FCSTD DOCUMENT  (FreeCAD 0.19R24366 (Git))
Label: hulltest2
License: All rights reserved
LicenseURL: http://en.wikipedia.org/wiki/All_rights_reserved
objects: Sketcher::SketchObject×3, PartDesign::Body×1
note: 4 computed .brp shape members not serialized (recipe doc carries the construction recipe); baked Part::Feature solids carry a one-line shape summary decoded from their .brp

FEATURE [Sketcher::SketchObject] Sketch  label="HullOutline"
  FullyConstrained = true
  Placement = pos=(0,0,0) rot=(0.980944,0.137386,0.137386;1.59004rad)
  Support = -> [XZ_Plane]
  sketch-geometry (8):
    g0: LineSegment StartX=0 StartY=0 StartZ=0 EndX=160 EndY=3 EndZ=0
    g1: LineSegment StartX=0 StartY=0 StartZ=0 EndX=-20 EndY=70 EndZ=0
    g2: LineSegment StartX=-20 StartY=70 StartZ=0 EndX=-170 EndY=70 EndZ=0
    g3: LineSegment StartX=-170 StartY=70 StartZ=0 EndX=-190 EndY=150 EndZ=0
    g4: LineSegment StartX=-190 StartY=150 StartZ=0 EndX=420 EndY=150 EndZ=0
    g5: LineSegment StartX=420 StartY=150 StartZ=0 EndX=180 EndY=70 EndZ=0
    g6: LineSegment StartX=180 StartY=70 StartZ=0 EndX=160 EndY=3 EndZ=0
    g7: LineSegment StartX=-20 StartY=70 StartZ=0 EndX=180 EndY=70 EndZ=0
  constraints (22):
    c: Coincident(g1,g0)
    c: Horizontal(g2)
    c: Coincident(g3,g2)
    c: Horizontal(g4)
    c: Coincident(g6,g5)
    c: Coincident(g6,g0)
    c: DistanceX(g4,g4) = 610
    c: Coincident(g3,g4)
    c: DistanceX(g3,g2) = 20
    c: DistanceX(g2,g1) = 150
    c: Coincident(g2,g1)
    c: DistanceY(g0,g1) = 70
    c: DistanceX(g0,g0) = 160
    c: DistanceX(g1,g0) = 20
    c: DistanceY(g2,g3) = 80
    c: DistanceY(g0,g0) = 3
    c: Horizontal(g1,g5)
    c: DistanceX(g0,g5) = 20
    c: Coincident(g5,g4)
    c: Coincident(g-1,g0)
    c: Coincident(g7,g1)
    c: Coincident(g7,g5)
FEATURE [Sketcher::SketchObject] Sketch004  label="Segment1"
  ExternalGeometry = -> [Sketch]
  FullyConstrained = true
  MapMode = 5
  Placement = pos=(0,0,0) rot=(0.57735,0.57735,0.57735;2.0944rad)
  Support = -> [YZ_Plane]
  sketch-geometry (36):
    g0: LineSegment StartX=0 StartY=90.7889 StartZ=0 EndX=0 EndY=61.1833 EndZ=0
    g1: LineSegment StartX=0 StartY=90.7889 StartZ=0 EndX=0 EndY=120.394 EndZ=0
    g2: LineSegment StartX=0 StartY=31.5778 StartZ=0 EndX=0 EndY=61.1833 EndZ=0
    g3: LineSegment StartX=0 StartY=31.5778 StartZ=0 EndX=0 EndY=1.9722 EndZ=0
    g4: LineSegment StartX=0 StartY=31.5778 StartZ=0 EndX=51.2783 EndY=31.5778 EndZ=0
    g5: LineSegment StartX=0 StartY=61.1833 StartZ=0 EndX=102.557 EndY=61.1833 EndZ=0
    g6: LineSegment StartX=0 StartY=90.7889 StartZ=0 EndX=130 EndY=90.7889 EndZ=0
    g7: LineSegment StartX=0 StartY=120.394 StartZ=0 EndX=136.742 EndY=120.394 EndZ=0
    g8: Circle CenterX=68.3711 CenterY=120.394 CenterZ=0 NormalX=0 NormalY=0 NormalZ=1 AngleXU=0 Radius=68.3711
    g9: LineSegment StartX=0 StartY=120.394 StartZ=0 EndX=0 EndY=150 EndZ=0
    g10: LineSegment StartX=0 StartY=150 StartZ=0 EndX=130 EndY=150 EndZ=0
    g11: LineSegment StartX=0 StartY=1.9722 StartZ=0 EndX=102.557 EndY=61.1833 EndZ=0
    g12: LineSegment StartX=0 StartY=61.1833 StartZ=0 EndX=0 EndY=90.7889 EndZ=0
    g13: LineSegment StartX=0 StartY=31.5778 StartZ=0 EndX=0 EndY=61.1833 EndZ=0
    g14: LineSegment StartX=-40 StartY=90.7889 StartZ=0 EndX=-40 EndY=61.1833 EndZ=0
    g15: LineSegment StartX=-40 StartY=90.7889 StartZ=0 EndX=-40 EndY=120.394 EndZ=0
    g16: LineSegment StartX=-40 StartY=31.5778 StartZ=0 EndX=-40 EndY=61.1833 EndZ=0
    g17: LineSegment StartX=-40 StartY=31.5778 StartZ=0 EndX=-40 EndY=1.9722 EndZ=0
    g18: LineSegment StartX=-40 StartY=31.5778 StartZ=0 EndX=-91.2783 EndY=31.5778 EndZ=0
    g19: LineSegment StartX=-40 StartY=61.1833 StartZ=0 EndX=-142.557 EndY=61.1833 EndZ=0
    g20: LineSegment StartX=-40 StartY=90.7889 StartZ=0 EndX=-170 EndY=90.7889 EndZ=0
    g21: LineSegment StartX=-40 StartY=120.394 StartZ=0 EndX=-176.742 EndY=120.394 EndZ=0
    g22: Circle CenterX=-108.371 CenterY=120.394 CenterZ=0 NormalX=0 NormalY=0 NormalZ=1 AngleXU=0 Radius=68.3711
    g23: LineSegment StartX=-40 StartY=120.394 StartZ=0 EndX=-40 EndY=150 EndZ=0
    g24: LineSegment StartX=-40 StartY=150 StartZ=0 EndX=-170 EndY=150 EndZ=0
    g25: LineSegment StartX=-40 StartY=61.1833 StartZ=0 EndX=-40 EndY=90.7889 EndZ=0
    g26: LineSegment StartX=-40 StartY=31.5778 StartZ=0 EndX=-40 EndY=61.1833 EndZ=0
    g27: LineSegment StartX=0 StartY=0 StartZ=0 EndX=-40 EndY=0 EndZ=0
    g28: LineSegment StartX=-142.557 StartY=61.1833 StartZ=0 EndX=-40 EndY=1.9722 EndZ=0
    g29: LineSegment StartX=-40 StartY=150 StartZ=0 EndX=0 EndY=150 EndZ=0
    g30: LineSegment StartX=-40 StartY=0 StartZ=0 EndX=-20 EndY=-9.32615 EndZ=0
    g31: LineSegment StartX=-20 StartY=-9.32615 StartZ=0 EndX=0 EndY=0 EndZ=0
    g32: LineSegment StartX=-40 StartY=1.9722 StartZ=0 EndX=-40 EndY=0 EndZ=0
    g33: LineSegment StartX=0 StartY=1.9722 StartZ=0 EndX=0 EndY=0 EndZ=0
    g34: LineSegment StartX=-40 StartY=150 StartZ=0 EndX=0 EndY=150 EndZ=0
    g35: LineSegment StartX=-170 StartY=150 StartZ=0 EndX=-40 EndY=150 EndZ=0
  constraints (102):
    c: PointOnObject(g10,g8)
    c: PointOnObject(g7,g8)
    c: PointOnObject(g5,g8)
    c: PointOnObject(g4,g11)
    c: Coincident(g9,g10)
    c: Coincident(g1,g7)
    c: Coincident(g1,g9)
    c: Coincident(g1,g6)
    c: Coincident(g1,g12)
    c: Coincident(g2,g3)
    c: Coincident(g2,g4)
    c: Coincident(g3,g11)
    c: Vertical(g3)
    c: Vertical(g2)
    c: Vertical(g0)
    c: Vertical(g12)
    c: Vertical(g1)
    c: Vertical(g9)
    c: Coincident(g0,g5)
    c: Horizontal(g4)
    c: Coincident(g5,g11)
    c: Horizontal(g5)
    c: Tangent(g11,g8)
    c: Horizontal(g6)
    c: Horizontal(g7)
    c: Horizontal(g10)
    c: Coincident(g0,g12)
    c: Equal(g3,g2)
    c: Equal(g2,g0)
    c: Equal(g0,g12)
    c: Equal(g12,g1)
    c: PointOnObject(g1,g8)
    c: Tangent(g1,g8)
    c: PointOnObject(g6,g8)
    c: Coincident(g13,g2)
    c: Coincident(g13,g0)
    c: Equal(g13,g0)
    c: Vertical(g13)
    c: Equal(g9,g1)
    c: PointOnObject(g24,g22)
    c: PointOnObject(g21,g22)
    c: PointOnObject(g19,g22)
    c: Coincident(g23,g24)
    c: Coincident(g15,g21)
    c: Coincident(g15,g23)
    c: Coincident(g15,g20)
    c: Coincident(g15,g25)
    c: Coincident(g16,g17)
    c: Coincident(g16,g18)
    c: Vertical(g17)
    c: Vertical(g16)
    c: Vertical(g14)
    c: Vertical(g25)
    c: Vertical(g15)
    c: Vertical(g23)
    c: Coincident(g14,g19)
    c: Horizontal(g18)
    c: Horizontal(g19)
    c: Horizontal(g20)
    c: Horizontal(g21)
    c: Horizontal(g24)
    c: Coincident(g14,g25)
    c: Equal(g16,g14)
    c: Equal(g14,g25)
    c: Equal(g25,g15)
    c: PointOnObject(g15,g22)
    c: Tangent(g15,g22)
    c: PointOnObject(g20,g22)
    c: Coincident(g26,g16)
    c: Coincident(g26,g14)
    c: Equal(g26,g14)
    c: Vertical(g26)
    c: Equal(g23,g15)
    c: Equal(g21,g7)
    c: Horizontal(g27)
    c: Coincident(g28,g19)
    c: Coincident(g28,g17)
    c: PointOnObject(g18,g28)
    c: Tangent(g28,g22)
    c: Coincident(g29,g23)
    c: Coincident(g29,g9)
    c: Horizontal(g29)
    c: Angle(g31,g30) = 2.26893
    c: Coincident(g30,g31)
    c: Coincident(g27,g30)
    c: Coincident(g31,g27)
    c: Coincident(g32,g17)
    c: Coincident(g32,g30)
    c: Vertical(g32)
    c: Coincident(g33,g3)
    c: Coincident(g33,g31)
    c: Vertical(g33)
    c: Coincident(g34,g23)
    c: Coincident(g35,g24)
    c: DistanceX(g27,g27) = 40
    c: DistanceX(g30,g31) = 20
    c: Coincident(g34,g9)
    c: Coincident(g35,g23)
    c: Horizontal(g-7,g9)
    c: Coincident(g-1,g31)
    c: DistanceX(g24,g10) = 300
    c: Horizontal(g2,g-3)
FEATURE [Sketcher::SketchObject] Sketch006  label="Segment002"
  ExternalGeometry = -> [Sketch]
  FullyConstrained = false
  MapMode = 1
  Placement = pos=(153.844,43.9554,3) rot=(0.57735,0.57735,0.57735;2.0944rad)
  Support = -> [Sketch]
  sketch-geometry (36):
    g0: LineSegment StartX=0 StartY=72.2178 StartZ=0 EndX=0 EndY=43.0677 EndZ=0
    g1: LineSegment StartX=0 StartY=72.2178 StartZ=0 EndX=0 EndY=101.368 EndZ=0
    g2: LineSegment StartX=0 StartY=13.9176 StartZ=0 EndX=0 EndY=43.0677 EndZ=0
    g3: LineSegment StartX=0 StartY=13.9176 StartZ=0 EndX=0 EndY=-15.2325 EndZ=0
    g4: LineSegment StartX=0 StartY=13.9176 StartZ=0 EndX=50.4894 EndY=13.9176 EndZ=0
    g5: LineSegment StartX=0 StartY=43.0677 StartZ=0 EndX=100.979 EndY=43.0677 EndZ=0
    g6: LineSegment StartX=0 StartY=72.2178 StartZ=0 EndX=128 EndY=72.2178 EndZ=0
    g7: LineSegment StartX=0 StartY=101.368 StartZ=0 EndX=134.638 EndY=101.368 EndZ=0
    g8: Circle CenterX=67.3192 CenterY=101.368 CenterZ=0 NormalX=0 NormalY=0 NormalZ=1 AngleXU=0 Radius=67.3192
    g9: LineSegment StartX=0 StartY=101.368 StartZ=0 EndX=0 EndY=130.518 EndZ=0
    g10: LineSegment StartX=0 StartY=130.518 StartZ=0 EndX=128 EndY=130.518 EndZ=0
    g11: LineSegment StartX=0 StartY=-15.2325 StartZ=0 EndX=100.979 EndY=43.0677 EndZ=0
    g12: LineSegment StartX=0 StartY=43.0677 StartZ=0 EndX=0 EndY=72.2178 EndZ=0
    g13: LineSegment StartX=0 StartY=13.9176 StartZ=0 EndX=0 EndY=43.0677 EndZ=0
    g14: LineSegment StartX=-40 StartY=72.2178 StartZ=0 EndX=-40 EndY=43.0677 EndZ=0
    g15: LineSegment StartX=-40 StartY=72.2178 StartZ=0 EndX=-40 EndY=101.368 EndZ=0
    g16: LineSegment StartX=-40 StartY=13.9176 StartZ=0 EndX=-40 EndY=43.0677 EndZ=0
    g17: LineSegment StartX=-40 StartY=13.9176 StartZ=0 EndX=-40 EndY=-15.2325 EndZ=0
    g18: LineSegment StartX=-40 StartY=13.9176 StartZ=0 EndX=-90.4894 EndY=13.9176 EndZ=0
    g19: LineSegment StartX=-40 StartY=43.0677 StartZ=0 EndX=-140.979 EndY=43.0677 EndZ=0
    g20: LineSegment StartX=-40 StartY=72.2178 StartZ=0 EndX=-168 EndY=72.2178 EndZ=0
    g21: LineSegment StartX=-40 StartY=101.368 StartZ=0 EndX=-174.638 EndY=101.368 EndZ=0
    g22: Circle CenterX=-107.319 CenterY=101.368 CenterZ=0 NormalX=0 NormalY=0 NormalZ=1 AngleXU=0 Radius=67.3192
    g23: LineSegment StartX=-40 StartY=101.368 StartZ=0 EndX=-40 EndY=130.518 EndZ=0
    g24: LineSegment StartX=-40 StartY=130.518 StartZ=0 EndX=-168 EndY=130.518 EndZ=0
    g25: LineSegment StartX=-40 StartY=43.0677 StartZ=0 EndX=-40 EndY=72.2178 EndZ=0
    g26: LineSegment StartX=-40 StartY=13.9176 StartZ=0 EndX=-40 EndY=43.0677 EndZ=0
    g27: LineSegment StartX=0 StartY=0 StartZ=0 EndX=-40 EndY=0 EndZ=0
    g28: LineSegment StartX=-140.979 StartY=43.0677 StartZ=0 EndX=-40 EndY=-15.2325 EndZ=0
    g29: LineSegment StartX=-40 StartY=130.518 StartZ=0 EndX=0 EndY=130.518 EndZ=0
    g30: LineSegment StartX=-40 StartY=0 StartZ=0 EndX=-20 EndY=-9.32615 EndZ=0
    g31: LineSegment StartX=-20 StartY=-9.32615 StartZ=0 EndX=0 EndY=0 EndZ=0
    g32: LineSegment StartX=-40 StartY=-15.2325 StartZ=0 EndX=-40 EndY=0 EndZ=0
    g33: LineSegment StartX=0 StartY=-15.2325 StartZ=0 EndX=0 EndY=0 EndZ=0
    g34: LineSegment StartX=-40 StartY=130.518 StartZ=0 EndX=0 EndY=130.518 EndZ=0
    g35: LineSegment StartX=-168 StartY=130.518 StartZ=0 EndX=-40 EndY=130.518 EndZ=0
  constraints (101):
    c: PointOnObject(g10,g8)
    c: PointOnObject(g7,g8)
    c: PointOnObject(g5,g8)
    c: PointOnObject(g4,g11)
    c: Coincident(g9,g10)
    c: Coincident(g1,g7)
    c: Coincident(g1,g9)
    c: Coincident(g1,g6)
    c: Coincident(g1,g12)
    c: Coincident(g2,g3)
    c: Coincident(g2,g4)
    c: Coincident(g3,g11)
    c: Vertical(g3)
    c: Vertical(g2)
    c: Vertical(g0)
    c: Vertical(g12)
    c: Vertical(g1)
    c: Vertical(g9)
    c: Coincident(g0,g5)
    c: Horizontal(g4)
    c: Coincident(g5,g11)
    c: Horizontal(g5)
    c: Tangent(g11,g8)
    c: Horizontal(g6)
    c: Horizontal(g7)
    c: Horizontal(g10)
    c: Coincident(g0,g12)
    c: Equal(g3,g2)
    c: Equal(g2,g0)
    c: Equal(g0,g12)
    c: Equal(g12,g1)
    c: PointOnObject(g1,g8)
    c: Tangent(g1,g8)
    c: PointOnObject(g6,g8)
    c: Coincident(g13,g2)
    c: Coincident(g13,g0)
    c: Equal(g13,g0)
    c: Vertical(g13)
    c: Equal(g9,g1)
    c: PointOnObject(g24,g22)
    c: PointOnObject(g21,g22)
    c: PointOnObject(g19,g22)
    c: Coincident(g23,g24)
    c: Coincident(g15,g21)
    c: Coincident(g15,g23)
    c: Coincident(g15,g20)
    c: Coincident(g15,g25)
    c: Coincident(g16,g17)
    c: Coincident(g16,g18)
    c: Vertical(g17)
    c: Vertical(g16)
    c: Vertical(g14)
    c: Vertical(g25)
    c: Vertical(g15)
    c: Vertical(g23)
    c: Coincident(g14,g19)
    c: Horizontal(g18)
    c: Horizontal(g19)
    c: Horizontal(g20)
    c: Horizontal(g21)
    c: Horizontal(g24)
    c: Coincident(g14,g25)
    c: Equal(g17,g16)
    c: Equal(g16,g14)
    c: Equal(g14,g25)
    c: Equal(g25,g15)
    c: PointOnObject(g15,g22)
    c: Tangent(g15,g22)
    c: PointOnObject(g20,g22)
    c: Coincident(g26,g16)
    c: Coincident(g26,g14)
    c: Equal(g26,g14)
    c: Vertical(g26)
    c: Equal(g23,g15)
    c: Equal(g21,g7)
    c: Horizontal(g27)
    c: Coincident(g28,g19)
    c: Coincident(g28,g17)
    c: PointOnObject(g18,g28)
    c: Tangent(g28,g22)
    c: Coincident(g29,g23)
    c: Coincident(g29,g9)
    c: Horizontal(g29)
    c: Angle(g31,g30) = 2.26893
    c: Coincident(g30,g31)
    c: Coincident(g27,g30)
    c: Coincident(g31,g27)
    c: Coincident(g32,g17)
    c: Coincident(g32,g30)
    c: Vertical(g32)
    c: Coincident(g33,g3)
    c: Coincident(g33,g31)
    c: Vertical(g33)
    c: Coincident(g34,g23)
    c: Coincident(g35,g24)
    c: DistanceX(g27,g27) = 40
    c: DistanceX(g30,g31) = 20
    c: Coincident(g34,g9)
    c: Coincident(g35,g23)
    c: Coincident(g-1,g31)
    c: DistanceX(g24,g10) = 296
FEATURE [PartDesign::Body] Body
  Group = -> [Sketch,Sketch004,Sketch006]
  Origin = -> Origin
